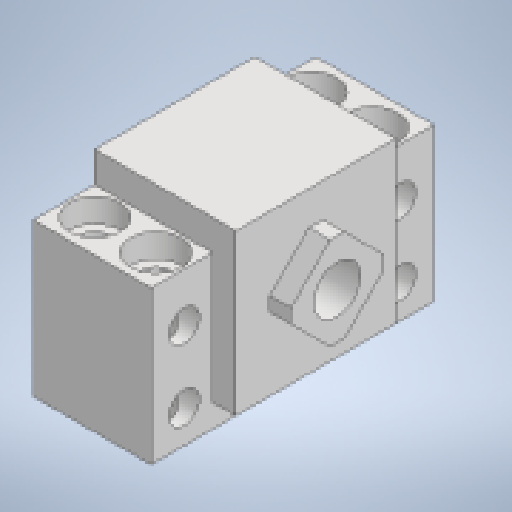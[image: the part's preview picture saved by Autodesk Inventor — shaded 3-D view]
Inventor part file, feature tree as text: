
AUTODESK INVENTOR PART (.ipt)
format: ipt  version: 2023 (Build 270158000, 158)  size: 238,080 bytes
history: native  units: mm
features: extrude x5, sketch x5, pattern_linear x1
ambient origin geometry x8: Origin, YZ Plane, XZ Plane, XY Plane, X Axis, Y Axis, Z Axis, Center Point
bodies: Solid1 (feature_tree)
feature tree (11):
  extrude  "Extrusion1"  Depth=60.0mm
  extrude  "Extrusion2"  Depth=46.0mm
  extrude  "Extrusion3"  Depth=32.5mm
  extrude  "Extrusion4"  Depth=39.0mm
  extrude  "Extrusion5"  Depth=25.0mm TaperAngle=0.0deg
  pattern_linear  "Rectangular Pattern1"  Spacing1=5.0mm  [1 undecoded]
  sketch  "Sketch1"  dims[d0=60.0mm d1=6.6mm]
  sketch  "Sketch2"  dims[d2=15.0mm d3=46.0mm]
  sketch  "Sketch3"  dims[d4=22.0mm d5=32.5mm]
  sketch  "Sketch4"  dims[d6=34.0mm d7=39.0mm]
  sketch  "Sketch5"  dims[d8=10.0mm d9=25.0mm d10=0.0mm d11=5.0mm d12=0.0mm d14=135.0deg d15=16.0mm d16=3.0mm d17=4.5mm d18=0.0mm d19=10.8mm d20=6.0mm d21=7.0mm d22=5.0mm d23=0.0mm d24=6.6mm d25=5.0mm d26=0.0mm d27=20.0mm d29=13.0mm d30=20.0mm d32=-46.0mm]
note: 1 required parameter value undecoded (feature->parameter linkage not recoverable at this tier; creation-order binding heuristic only, values carry confidence <= 0.55)
